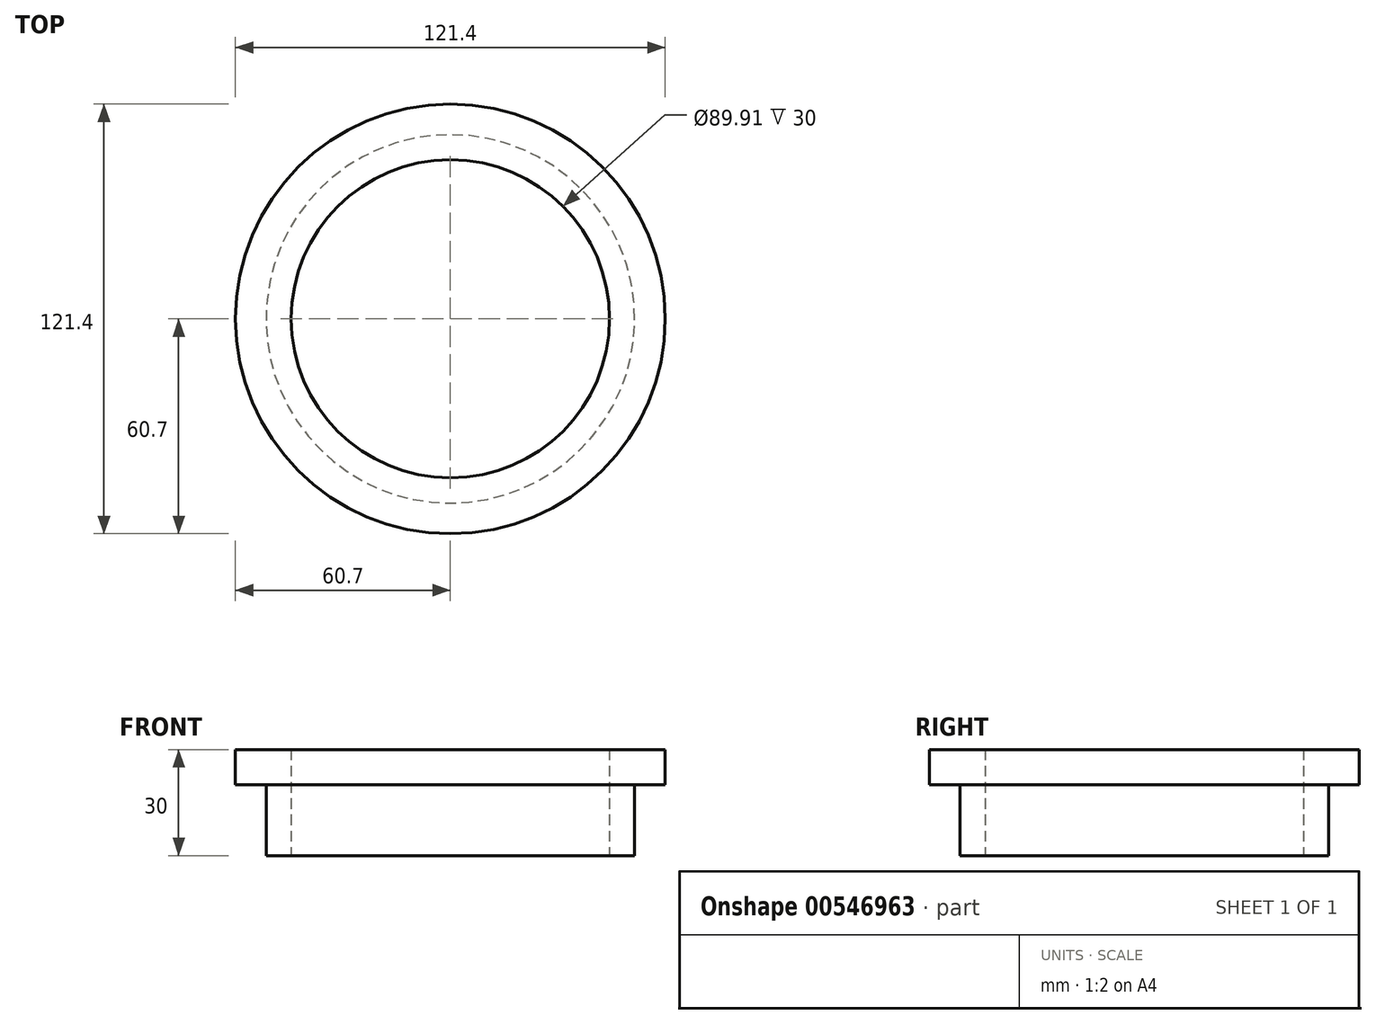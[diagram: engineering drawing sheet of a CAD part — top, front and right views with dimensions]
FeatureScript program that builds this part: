
annotation { "Feature Type Name" : "Feature", "Feature Type Description" : "" }
export const myFeature = defineFeature(function(context is Context, id is Id, definition is map)
    precondition{}
    {
        {
            var Q0;
            Q0=qCreatedBy(makeId("Top.planeOp"),FACE);
            var sketch = newSketch(context, id + "F0", { "sketchPlane" : qUnion([Q0])});
            skCircle(sketch, "E0", {"center": v(0, 0) * mm, "radius": 52.06 * mm});
            skCircle(sketch, "E1", {"center": v(0, 0) * mm, "radius": 44.95 * mm});
            skSolve(sketch);
        }
        {
            var Q0;
            Q0=makeQuery(id+"F0.imprint","IMPRINT",FACE,{"disambiguationData":[TD([[makeQuery(id+"F0.imprint","IMPRINT",EDGE,{"derivedFrom":sQuery(id+"F0.wireOp",EDGE,"E0")}),1.0]])]});
            extrude(context, id + "F1", {"entities" : qUnion([Q0]), "depth" : 20 * mm, "offsetDistance" : 25 * mm});
        }
        {
            var Q0;
            Q0=makeQuery(id+"F1.opExtrude","CAP_FACE",FACE,{"disambiguationData":[OSD([sQuery(id+"F0.wireOp",EDGE,"E0"),sQuery(id+"F0.wireOp",EDGE,"E1")])],"isStart":false});
            var sketch = newSketch(context, id + "F2", { "sketchPlane" : qUnion([Q0])});
            skCircle(sketch, "E2", {"center": v(0, 0) * mm, "radius": 60.7 * mm});
            skSolve(sketch);
        }
        {
            var Q0;
            Q0=makeQuery(id+"F2.imprint","IMPRINT",FACE,{"disambiguationData":[TD([[makeQuery(id+"F2.imprint","IMPRINT",EDGE,{"derivedFrom":sQuery(id+"F2.wireOp",EDGE,"E2")}),1.0]])]});
            var Q1;
            Q1=makeQuery(id+"F2.imprint","IMPRINT",FACE,{"disambiguationData":[TD([[makeQuery(id+"F2.imprint","IMPRINT",EDGE,{"derivedFrom":makeQuery(id+"F1.opExtrude","CAP_EDGE",EDGE,{"disambiguationData":[OSD([sQuery(id+"F0.wireOp",EDGE,"E0")])],"isStart":false})}),1.0]])]});
            extrude(context, id + "F3", {"entities" : qUnion([Q0, Q1]), "operationType" : NewBodyOperationType.ADD, "depth" : 10 * mm, "offsetDistance" : 25 * mm});
        }
    });
